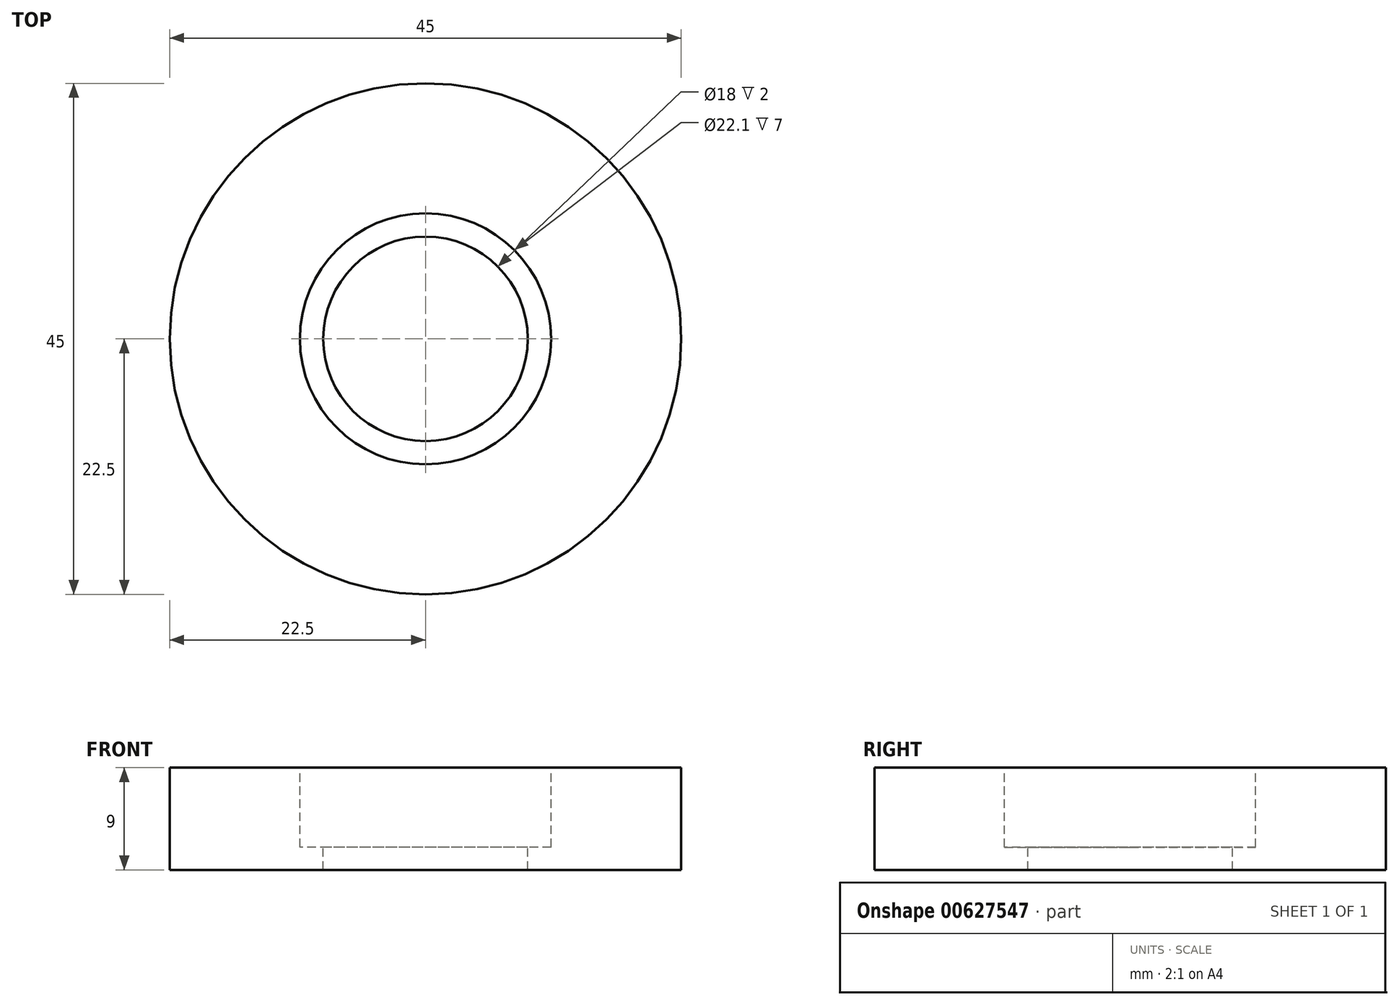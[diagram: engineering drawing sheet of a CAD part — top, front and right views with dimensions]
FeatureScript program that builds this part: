
annotation { "Feature Type Name" : "Feature", "Feature Type Description" : "" }
export const myFeature = defineFeature(function(context is Context, id is Id, definition is map)
    precondition{}
    {
        {
            var Q0;
            Q0=qCreatedBy(makeId("Top.planeOp"),FACE);
            var sketch = newSketch(context, id + "F0", { "sketchPlane" : qUnion([Q0])});
            skCircle(sketch, "E0", {"center": v(0, 0) * mm, "radius": 22.5 * mm});
            skSolve(sketch);
        }
        {
            var Q0;
            Q0=qSketchRegion(id+"F0",true);
            extrude(context, id + "F1", {"entities" : qUnion([Q0]), "depth" : 9 * mm, "offsetDistance" : 25 * mm});
        }
        {
            var Q0;
            Q0=makeQuery(id+"F1.opExtrude","CAP_FACE",FACE,{"disambiguationData":[OSD([sQuery(id+"F0.wireOp",EDGE,"E0")])],"isStart":false});
            var sketch = newSketch(context, id + "F2", { "sketchPlane" : qUnion([Q0])});
            skCircle(sketch, "E1", {"center": v(0, 0) * mm, "radius": 9 * mm});
            skSolve(sketch);
        }
        {
            var Q0;
            Q0=qSketchRegion(id+"F2",true);
            extrude(context, id + "F3", {"entities" : qUnion([Q0]), "operationType" : NewBodyOperationType.REMOVE, "endBound" : BoundingType.THROUGH_ALL, "oppositeDirection" : true, "depth" : 25 * mm, "offsetDistance" : 25 * mm});
        }
        {
            var Q0;
            Q0=makeQuery(id+"F1.opExtrude","CAP_FACE",FACE,{"disambiguationData":[OSD([sQuery(id+"F0.wireOp",EDGE,"E0")])],"isStart":false});
            var sketch = newSketch(context, id + "F4", { "sketchPlane" : qUnion([Q0])});
            skCircle(sketch, "E2", {"center": v(0, 0) * mm, "radius": 11.05 * mm});
            skSolve(sketch);
        }
        {
            var Q0;
            Q0=qSketchRegion(id+"F4",true);
            extrude(context, id + "F5", {"entities" : qUnion([Q0]), "operationType" : NewBodyOperationType.REMOVE, "oppositeDirection" : true, "depth" : 7 * mm, "offsetDistance" : 25 * mm});
        }
    });
